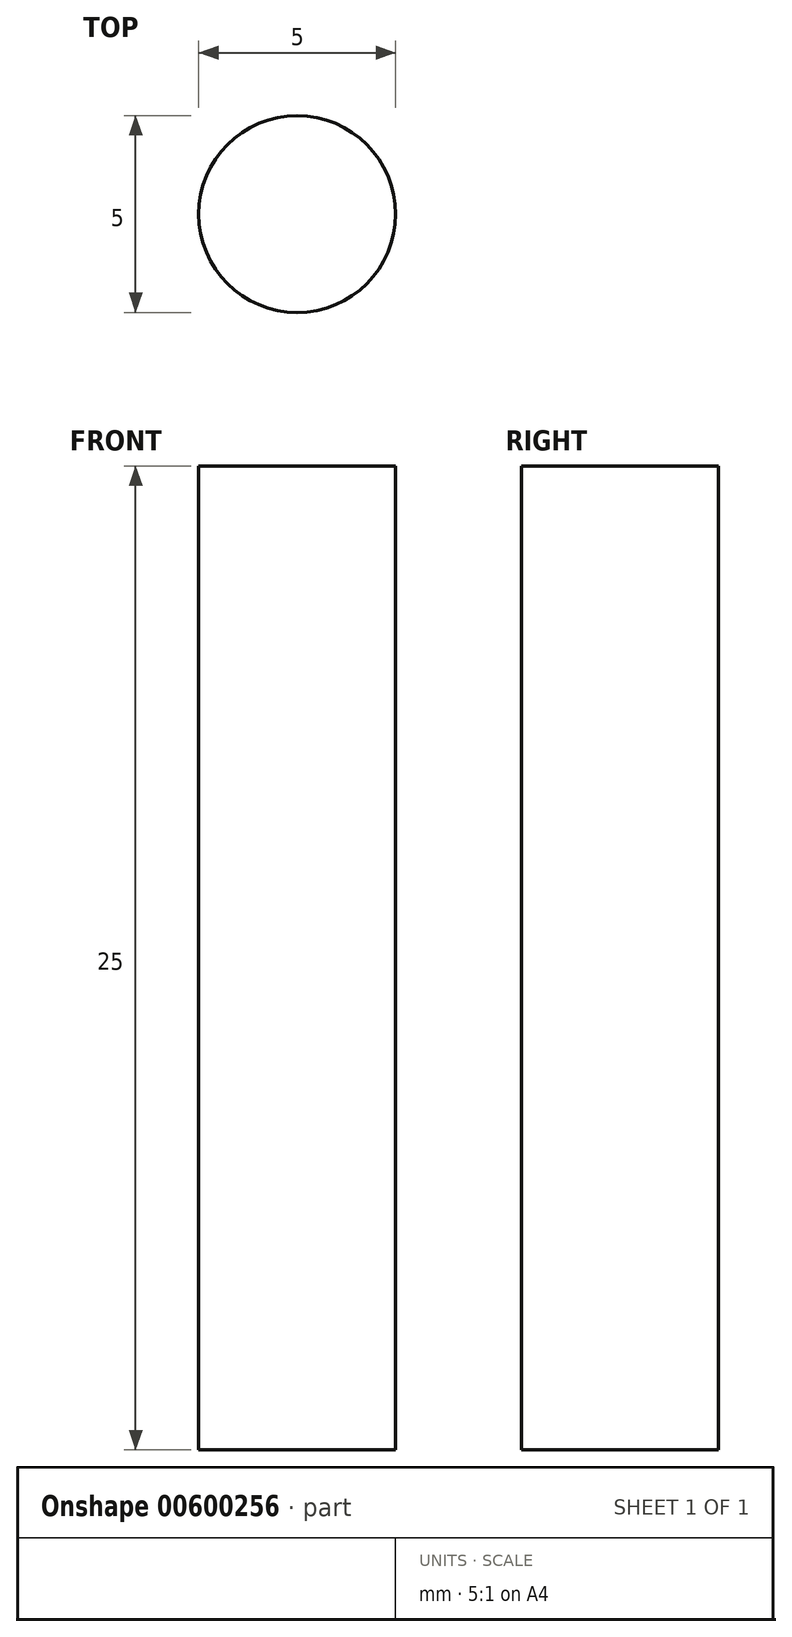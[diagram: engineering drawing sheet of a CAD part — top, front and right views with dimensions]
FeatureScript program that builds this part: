
annotation { "Feature Type Name" : "Feature", "Feature Type Description" : "" }
export const myFeature = defineFeature(function(context is Context, id is Id, definition is map)
    precondition{}
    {
        {
            var Q0;
            Q0=qCreatedBy(makeId("Top.planeOp"),FACE);
            var sketch = newSketch(context, id + "F0", { "sketchPlane" : qUnion([Q0])});
            skCircle(sketch, "E0", {"center": v(0, 0) * mm, "radius": 2.5 * mm});
            skSolve(sketch);
        }
        {
            var Q0;
            Q0 = qSketchRegion(id + "F0", true);
            extrude(context, id + "F1", {"entities" : qUnion([Q0]), "depth" : 25 * mm, "offsetDistance" : 25 * mm});
        }
    });
